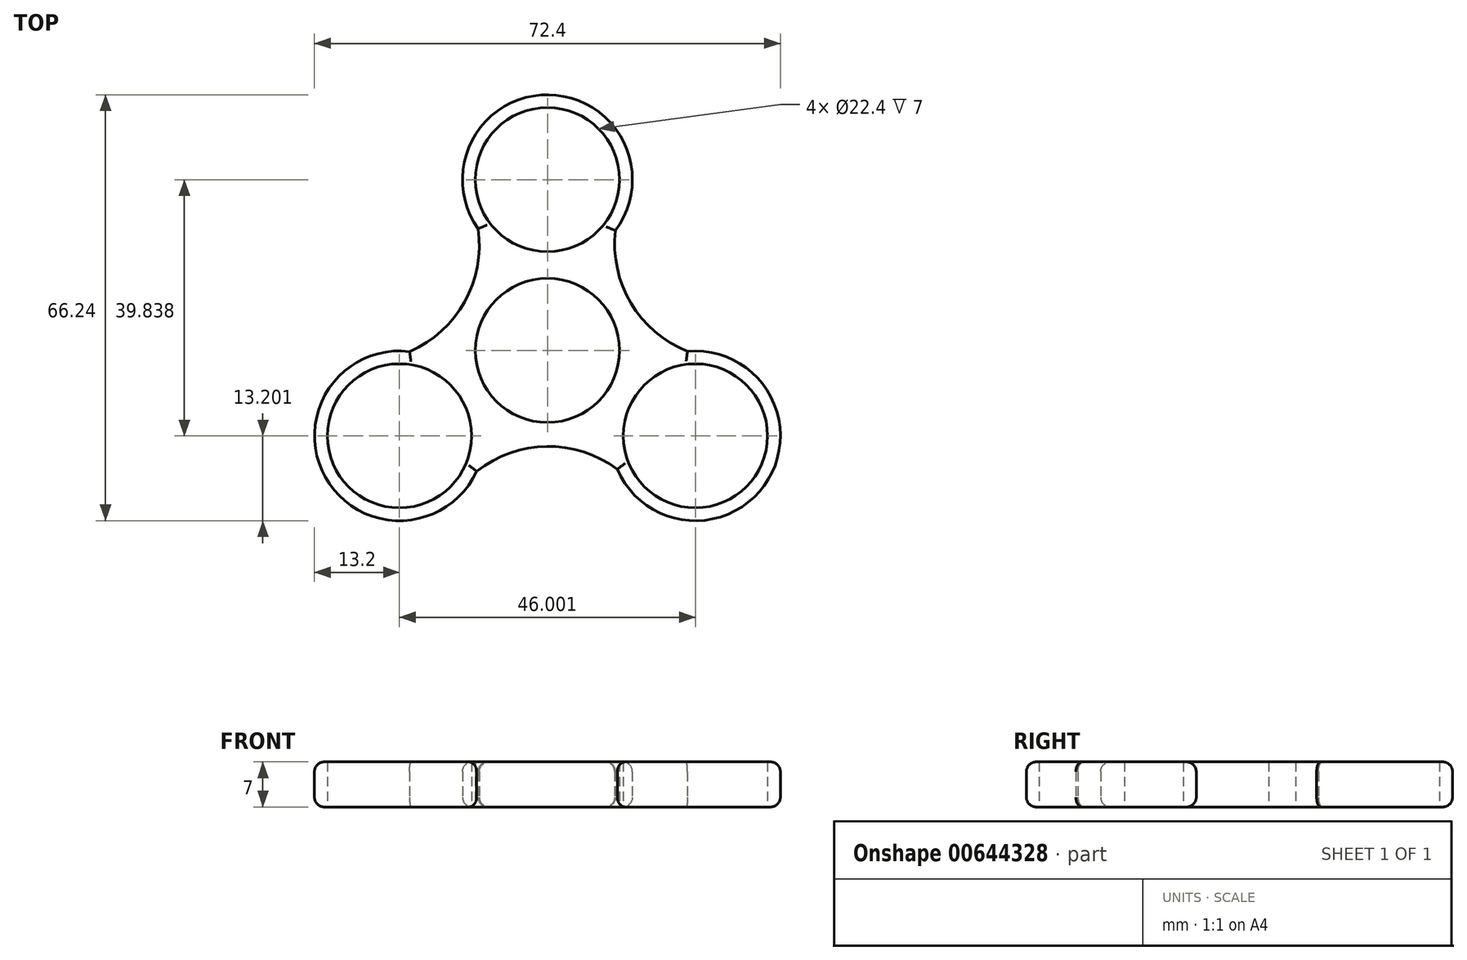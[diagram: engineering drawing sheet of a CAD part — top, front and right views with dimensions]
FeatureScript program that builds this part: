
annotation { "Feature Type Name" : "Feature", "Feature Type Description" : "" }
export const myFeature = defineFeature(function(context is Context, id is Id, definition is map)
    precondition{}
    {
        {
            var Q0;
            Q0=qCreatedBy(makeId("Top.planeOp"),FACE);
            var sketch = newSketch(context, id + "F0", { "sketchPlane" : qUnion([Q0])});
            skCircle(sketch, "E0", {"center": v(0, 0) * mm, "radius": 11.2 * mm});
            skCircle(sketch, "E1", {"center": v(0, 26.56) * mm, "radius": 11.2 * mm});
            skArc(sketch, "E2", {"start": v(10.56, 18.64) * mm, "mid": v(0.17, 39.76) * mm, "end": v(-10.77, 18.92) * mm});
            skArc(sketch, "E3.1.0", {"start": v(-21.43, -0.17) * mm, "mid": v(-34.52, -19.73) * mm, "end": v(-11, -18.78) * mm});
            skCircle(sketch, "E3.1.1", {"center": v(-23, -13.28) * mm, "radius": 11.2 * mm});
            skArc(sketch, "E3.2.0", {"start": v(10.86, -18.47) * mm, "mid": v(34.34, -20.03) * mm, "end": v(21.77, -0.14) * mm});
            skCircle(sketch, "E3.2.1", {"center": v(23, -13.28) * mm, "radius": 11.2 * mm});
            skLineSegment(sketch, "E4", {"start": v(-0.64, -0.37) * mm, "end": v(0, 0) * mm, "construction": true});
            skArc(sketch, "E5", {"start": v(10.56, 18.64) * mm, "mid": v(12.99, 7.36) * mm, "end": v(21.77, -0.14) * mm});
            skArc(sketch, "E6.1.0", {"start": v(-21.43, -0.17) * mm, "mid": v(-12.86, 7.57) * mm, "end": v(-10.77, 18.92) * mm});
            skArc(sketch, "E6.2.0", {"start": v(10.86, -18.47) * mm, "mid": v(-0.12, -14.92) * mm, "end": v(-11, -18.78) * mm});
            skSolve(sketch);
        }
        {
            var Q0;
            Q0=makeQuery(id+"F0.imprint","IMPRINT",FACE,{"disambiguationData":[TD([[makeQuery(id+"F0.imprint","IMPRINT",EDGE,{"derivedFrom":sQuery(id+"F0.wireOp",EDGE,"E0")}),-1.0]])]});
            extrude(context, id + "F1", {"entities" : qUnion([Q0]), "depth" : 7 * mm, "offsetDistance" : 25 * mm});
        }
        {
            var Q0;
            Q0=makeQuery(id+"F1.opExtrude","CAP_EDGE",EDGE,{"disambiguationData":[OSD([sQuery(id+"F0.wireOp",EDGE,"E3.1.0")])],"isStart":false});
            var Q1;
            Q1=makeQuery(id+"F1.opExtrude","CAP_EDGE",EDGE,{"disambiguationData":[OSD([sQuery(id+"F0.wireOp",EDGE,"E6.2.0")])],"isStart":false});
            var Q2;
            Q2=makeQuery(id+"F1.opExtrude","CAP_EDGE",EDGE,{"disambiguationData":[OSD([sQuery(id+"F0.wireOp",EDGE,"E6.1.0")])],"isStart":false});
            var Q3;
            Q3=makeQuery(id+"F1.opExtrude","CAP_EDGE",EDGE,{"disambiguationData":[OSD([sQuery(id+"F0.wireOp",EDGE,"E2")])],"isStart":false});
            var Q4;
            Q4=makeQuery(id+"F1.opExtrude","CAP_EDGE",EDGE,{"disambiguationData":[OSD([sQuery(id+"F0.wireOp",EDGE,"E5")])],"isStart":false});
            var Q5;
            Q5=makeQuery(id+"F1.opExtrude","CAP_EDGE",EDGE,{"disambiguationData":[OSD([sQuery(id+"F0.wireOp",EDGE,"E3.2.0")])],"isStart":false});
            var Q6;
            Q6=makeQuery(id+"F1.opExtrude","CAP_EDGE",EDGE,{"disambiguationData":[OSD([sQuery(id+"F0.wireOp",EDGE,"E5")])],"isStart":true});
            var Q7;
            Q7=makeQuery(id+"F1.opExtrude","CAP_EDGE",EDGE,{"disambiguationData":[OSD([sQuery(id+"F0.wireOp",EDGE,"E3.2.0")])],"isStart":true});
            var Q8;
            Q8=makeQuery(id+"F1.opExtrude","CAP_EDGE",EDGE,{"disambiguationData":[OSD([sQuery(id+"F0.wireOp",EDGE,"E6.2.0")])],"isStart":true});
            var Q9;
            Q9=makeQuery(id+"F1.opExtrude","CAP_EDGE",EDGE,{"disambiguationData":[OSD([sQuery(id+"F0.wireOp",EDGE,"E3.1.0")])],"isStart":true});
            var Q10;
            Q10=makeQuery(id+"F1.opExtrude","CAP_EDGE",EDGE,{"disambiguationData":[OSD([sQuery(id+"F0.wireOp",EDGE,"E6.1.0")])],"isStart":true});
            var Q11;
            Q11=makeQuery(id+"F1.opExtrude","CAP_EDGE",EDGE,{"disambiguationData":[OSD([sQuery(id+"F0.wireOp",EDGE,"E2")])],"isStart":true});
            fillet(context, id + "F2", {"entities" : qUnion([Q0, Q1, Q2, Q3, Q4, Q5, Q6, Q7, Q8, Q9, Q10, Q11]), "radius" : 1.5 * mm, "tangentPropagation" : true, "allowEdgeOverflow" : false});
        }
    });
